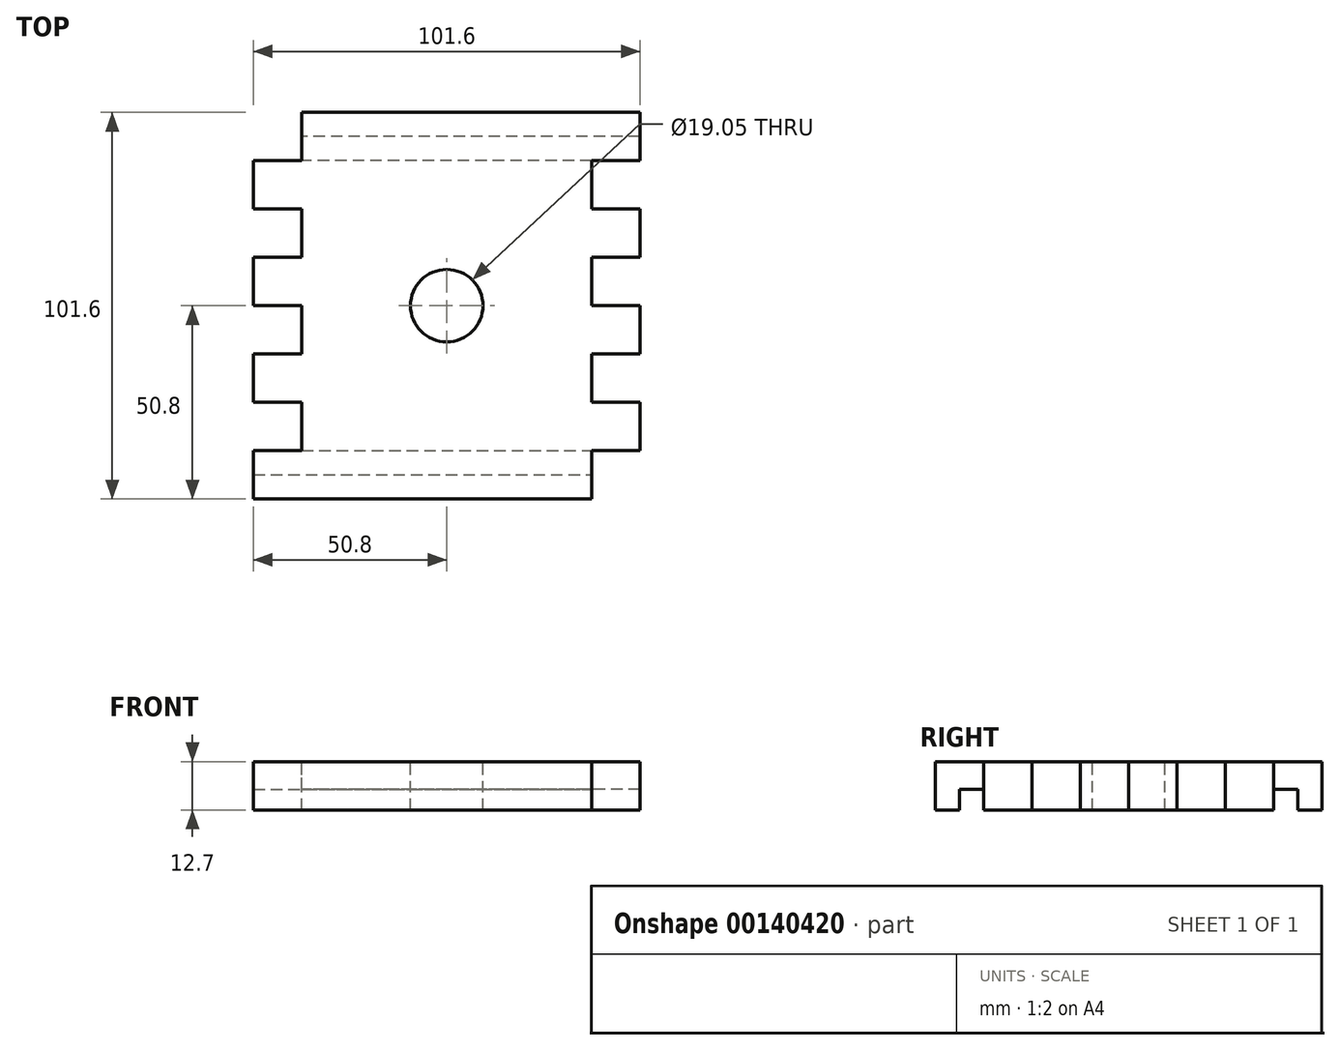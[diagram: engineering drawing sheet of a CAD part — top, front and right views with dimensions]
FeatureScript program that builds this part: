
annotation { "Feature Type Name" : "Feature", "Feature Type Description" : "" }
export const myFeature = defineFeature(function(context is Context, id is Id, definition is map)
    precondition{}
    {
        {
            var Q0;
            Q0=qCreatedBy(makeId("Top.planeOp"),FACE);
            var sketch = newSketch(context, id + "F0", { "sketchPlane" : qUnion([Q0])});
            skLineSegment(sketch, "E0.bottom", {"start": v(50.8, 50.8) * mm, "end": v(-50.8, 50.8) * mm});
            skLineSegment(sketch, "E0.top", {"start": v(50.8, -50.8) * mm, "end": v(-50.8, -50.8) * mm});
            skLineSegment(sketch, "E0.left", {"start": v(50.8, 50.8) * mm, "end": v(50.8, -50.8) * mm});
            skLineSegment(sketch, "E0.right", {"start": v(-50.8, 50.8) * mm, "end": v(-50.8, -50.8) * mm});
            skPoint(sketch, "E0.middle", {"position": v(0, 0) * mm});
            skSolve(sketch);
        }
        {
            var Q0;
            Q0=makeQuery(id+"F0.imprint","IMPRINT",FACE,{"disambiguationData":[TD([[makeQuery(id+"F0.imprint","IMPRINT",EDGE,{"derivedFrom":sQuery(id+"F0.wireOp",EDGE,"E0.bottom")}),1.0]])]});
            extrude(context, id + "F1", {"entities" : qUnion([Q0]), "depth" : 12.7 * mm});
        }
        {
            var Q0;
            Q0=makeQuery(id+"F1.opExtrude","CAP_FACE",FACE,{"disambiguationData":[OSD([sQuery(id+"F0.wireOp",EDGE,"E0.bottom"),sQuery(id+"F0.wireOp",EDGE,"E0.top"),sQuery(id+"F0.wireOp",EDGE,"E0.left"),sQuery(id+"F0.wireOp",EDGE,"E0.right")])],"isStart":false});
            var sketch = newSketch(context, id + "F2", { "sketchPlane" : qUnion([Q0])});
            skLineSegment(sketch, "E1", {"start": v(-50.8, 50.8) * mm, "end": v(-38.1, 50.8) * mm});
            skLineSegment(sketch, "E2", {"start": v(-38.1, 50.8) * mm, "end": v(-38.1, 38.1) * mm});
            skLineSegment(sketch, "E3", {"start": v(-38.1, 38.1) * mm, "end": v(-50.8, 38.1) * mm});
            skLineSegment(sketch, "E4", {"start": v(-50.8, 38.1) * mm, "end": v(-50.8, 25.4) * mm});
            skLineSegment(sketch, "E5", {"start": v(-50.8, 25.4) * mm, "end": v(-38.1, 25.4) * mm});
            skLineSegment(sketch, "E6", {"start": v(-38.1, 25.4) * mm, "end": v(-38.1, 12.7) * mm});
            skLineSegment(sketch, "E7", {"start": v(-38.1, 12.7) * mm, "end": v(-50.8, 12.7) * mm});
            skLineSegment(sketch, "E8", {"start": v(-50.8, 12.7) * mm, "end": v(-50.8, 0) * mm});
            skLineSegment(sketch, "E9", {"start": v(-50.8, 0) * mm, "end": v(-38.1, 0) * mm});
            skLineSegment(sketch, "E10", {"start": v(-38.1, 0) * mm, "end": v(-38.1, -12.7) * mm});
            skLineSegment(sketch, "E11", {"start": v(-38.1, -12.7) * mm, "end": v(-50.8, -12.7) * mm});
            skLineSegment(sketch, "E12", {"start": v(-50.8, -12.7) * mm, "end": v(-50.8, -25.4) * mm});
            skLineSegment(sketch, "E13", {"start": v(-50.8, -25.4) * mm, "end": v(-38.1, -25.4) * mm});
            skLineSegment(sketch, "E14", {"start": v(-38.1, -25.4) * mm, "end": v(-38.1, -38.1) * mm});
            skLineSegment(sketch, "E15", {"start": v(-38.1, -38.1) * mm, "end": v(-50.8, -38.1) * mm});
            skSolve(sketch);
        }
        {
            var Q0;
            {var subQ0=sQuery(id+"F2.wireOp",EDGE,"E5");Q0=makeQuery(id+"F2.imprint","IMPRINT",FACE,{"disambiguationData":[TD([[makeQuery(id+"F2.imprint","IMPRINT",EDGE,{"derivedFrom":subQ0}),-1.0]])]});}
            var Q1;
            {var subQ0=sQuery(id+"F2.wireOp",EDGE,"E1");Q1=makeQuery(id+"F2.imprint","IMPRINT",FACE,{"disambiguationData":[TD([[makeQuery(id+"F2.imprint","IMPRINT",EDGE,{"derivedFrom":subQ0}),1.0]])]});}
            var Q2;
            {var subQ0=sQuery(id+"F2.wireOp",EDGE,"E9");Q2=makeQuery(id+"F2.imprint","IMPRINT",FACE,{"disambiguationData":[TD([[makeQuery(id+"F2.imprint","IMPRINT",EDGE,{"derivedFrom":subQ0}),-1.0]])]});}
            var Q3;
            {var subQ0=sQuery(id+"F2.wireOp",EDGE,"E13");Q3=makeQuery(id+"F2.imprint","IMPRINT",FACE,{"disambiguationData":[TD([[makeQuery(id+"F2.imprint","IMPRINT",EDGE,{"derivedFrom":subQ0}),-1.0]])]});}
            extrude(context, id + "F3", {"entities" : qUnion([Q0, Q1, Q2, Q3]), "operationType" : NewBodyOperationType.REMOVE, "endBound" : BoundingType.THROUGH_ALL, "oppositeDirection" : true, "depth" : 25.4 * mm});
        }
        {
            var Q0;
            Q0=makeQuery(id+"F1.opExtrude","CAP_FACE",FACE,{"disambiguationData":[OSD([sQuery(id+"F0.wireOp",EDGE,"E0.bottom"),sQuery(id+"F0.wireOp",EDGE,"E0.top"),sQuery(id+"F0.wireOp",EDGE,"E0.left"),sQuery(id+"F0.wireOp",EDGE,"E0.right")])],"isStart":false});
            var sketch = newSketch(context, id + "F4", { "sketchPlane" : qUnion([Q0])});
            skLineSegment(sketch, "E16", {"start": v(50.8, -50.8) * mm, "end": v(38.1, -50.8) * mm});
            skLineSegment(sketch, "E17", {"start": v(38.1, -50.8) * mm, "end": v(38.1, -38.1) * mm});
            skLineSegment(sketch, "E18", {"start": v(38.1, -38.1) * mm, "end": v(50.8, -38.1) * mm});
            skLineSegment(sketch, "E19", {"start": v(50.8, -38.1) * mm, "end": v(50.8, -25.4) * mm});
            skLineSegment(sketch, "E20", {"start": v(50.8, -25.4) * mm, "end": v(38.1, -25.4) * mm});
            skLineSegment(sketch, "E21", {"start": v(38.1, -25.4) * mm, "end": v(38.1, -12.7) * mm});
            skLineSegment(sketch, "E22", {"start": v(38.1, -12.7) * mm, "end": v(50.8, -12.7) * mm});
            skLineSegment(sketch, "E23", {"start": v(50.8, -12.7) * mm, "end": v(50.8, 0) * mm});
            skLineSegment(sketch, "E24", {"start": v(50.8, 0) * mm, "end": v(38.1, 0) * mm});
            skLineSegment(sketch, "E25", {"start": v(38.1, 0) * mm, "end": v(38.1, 12.7) * mm});
            skLineSegment(sketch, "E26", {"start": v(38.1, 12.7) * mm, "end": v(50.8, 12.7) * mm});
            skLineSegment(sketch, "E27", {"start": v(50.8, 12.7) * mm, "end": v(50.8, 25.4) * mm});
            skLineSegment(sketch, "E28", {"start": v(50.8, 25.4) * mm, "end": v(38.1, 25.4) * mm});
            skLineSegment(sketch, "E29", {"start": v(38.1, 25.4) * mm, "end": v(38.1, 38.1) * mm});
            skLineSegment(sketch, "E30", {"start": v(38.1, 38.1) * mm, "end": v(50.8, 38.1) * mm});
            skSolve(sketch);
        }
        {
            var Q0;
            {var subQ0=sQuery(id+"F4.wireOp",EDGE,"E28");Q0=makeQuery(id+"F4.imprint","IMPRINT",FACE,{"disambiguationData":[TD([[makeQuery(id+"F4.imprint","IMPRINT",EDGE,{"derivedFrom":subQ0}),-1.0]])]});}
            var Q1;
            {var subQ0=sQuery(id+"F4.wireOp",EDGE,"E24");Q1=makeQuery(id+"F4.imprint","IMPRINT",FACE,{"disambiguationData":[TD([[makeQuery(id+"F4.imprint","IMPRINT",EDGE,{"derivedFrom":subQ0}),-1.0]])]});}
            var Q2;
            {var subQ0=sQuery(id+"F4.wireOp",EDGE,"E20");Q2=makeQuery(id+"F4.imprint","IMPRINT",FACE,{"disambiguationData":[TD([[makeQuery(id+"F4.imprint","IMPRINT",EDGE,{"derivedFrom":subQ0}),-1.0]])]});}
            var Q3;
            {var subQ0=sQuery(id+"F4.wireOp",EDGE,"E16");Q3=makeQuery(id+"F4.imprint","IMPRINT",FACE,{"disambiguationData":[TD([[makeQuery(id+"F4.imprint","IMPRINT",EDGE,{"derivedFrom":subQ0}),-1.0]])]});}
            extrude(context, id + "F5", {"entities" : qUnion([Q0, Q1, Q2, Q3]), "operationType" : NewBodyOperationType.REMOVE, "endBound" : BoundingType.THROUGH_ALL, "oppositeDirection" : true, "depth" : 25.4 * mm});
        }
        {
            var Q0;
            Q0=makeQuery(id+"F5.boolean.opBoolean","COPY",FACE,{"derivedFrom":makeQuery(id+"F5.opExtrude","SWEPT_FACE",FACE,{"disambiguationData":[OSD([sQuery(id+"F4.wireOp",EDGE,"E17")])]})});
            var sketch = newSketch(context, id + "F6", { "sketchPlane" : qUnion([Q0])});
            skLineSegment(sketch, "E31", {"start": v(-44.45, 0) * mm, "end": v(-44.45, 5.42) * mm});
            skLineSegment(sketch, "E32", {"start": v(-44.45, 5.42) * mm, "end": v(-38.1, 5.42) * mm});
            skSolve(sketch);
        }
        {
            var Q0;
            {var subQ0=sQuery(id+"F6.wireOp",EDGE,"E31");Q0=makeQuery(id+"F6.imprint","IMPRINT",FACE,{"disambiguationData":[TD([[makeQuery(id+"F6.imprint","IMPRINT",EDGE,{"derivedFrom":subQ0}),-1.0]])]});}
            extrude(context, id + "F7", {"entities" : qUnion([Q0]), "operationType" : NewBodyOperationType.REMOVE, "endBound" : BoundingType.THROUGH_ALL, "oppositeDirection" : true, "depth" : 25.4 * mm});
        }
        {
            var Q0;
            Q0=makeQuery(id+"F3.boolean.opBoolean","COPY",FACE,{"derivedFrom":makeQuery(id+"F3.opExtrude","SWEPT_FACE",FACE,{"disambiguationData":[OSD([sQuery(id+"F2.wireOp",EDGE,"E2")])]})});
            var sketch = newSketch(context, id + "F8", { "sketchPlane" : qUnion([Q0])});
            skLineSegment(sketch, "E33", {"start": v(-44.45, 0) * mm, "end": v(-44.45, 5.39) * mm});
            skLineSegment(sketch, "E34", {"start": v(-44.45, 5.39) * mm, "end": v(-38.1, 5.39) * mm});
            skPoint(sketch, "E34.endSnap0", {"position": v(-38.1, 6.35) * mm});
            skSolve(sketch);
        }
        {
            var Q0;
            {var subQ0=sQuery(id+"F8.wireOp",EDGE,"E33");Q0=makeQuery(id+"F8.imprint","IMPRINT",FACE,{"disambiguationData":[TD([[makeQuery(id+"F8.imprint","IMPRINT",EDGE,{"derivedFrom":subQ0}),-1.0]])]});}
            extrude(context, id + "F9", {"entities" : qUnion([Q0]), "operationType" : NewBodyOperationType.REMOVE, "endBound" : BoundingType.THROUGH_ALL, "oppositeDirection" : true, "depth" : 25.4 * mm});
        }
        {
            var Q0;
            Q0=makeQuery(id+"F1.opExtrude","CAP_FACE",FACE,{"disambiguationData":[OSD([sQuery(id+"F0.wireOp",EDGE,"E0.bottom"),sQuery(id+"F0.wireOp",EDGE,"E0.top"),sQuery(id+"F0.wireOp",EDGE,"E0.left"),sQuery(id+"F0.wireOp",EDGE,"E0.right")])],"isStart":false});
            var sketch = newSketch(context, id + "F10", { "sketchPlane" : qUnion([Q0])});
            skCircle(sketch, "E35", {"center": v(0, 0) * mm, "radius": 9.53 * mm});
            skSolve(sketch);
        }
        {
            var Q0;
            Q0=makeQuery(id+"F10.imprint","IMPRINT",FACE,{"disambiguationData":[TD([[makeQuery(id+"F10.imprint","IMPRINT",EDGE,{"derivedFrom":sQuery(id+"F10.wireOp",EDGE,"E35")}),1.0]])]});
            extrude(context, id + "F11", {"entities" : qUnion([Q0]), "operationType" : NewBodyOperationType.REMOVE, "endBound" : BoundingType.THROUGH_ALL, "oppositeDirection" : true, "depth" : 25.4 * mm});
        }
    });
